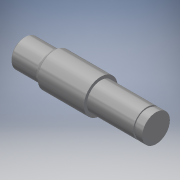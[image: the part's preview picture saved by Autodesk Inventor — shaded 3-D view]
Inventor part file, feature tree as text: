
AUTODESK INVENTOR PART (.ipt)
format: ipt  version: 2019 (Build 230136000, 136)  size: 138,240 bytes
history: native  units: mm
features: other x6, chamfer x1, fillet x1
ambient origin geometry x6: Origin, XZ Plane, XY Plane, X Axis, Y Axis, Z Axis
bodies: Body1 (feature_tree)
feature tree (8):
  other  "實體1"
  other  "迴轉1"
  chamfer  "倒角1"  [1 undecoded]
  fillet  "圓角1"  Radius=9.0mm
  other  "扣環槽1"
  other  "起始平面"
  other  "主要草圖"
  other  "iFeature27:1"
note: 1 required parameter value undecoded (feature->parameter linkage not recoverable at this tier; creation-order binding heuristic only, values carry confidence <= 0.55)
